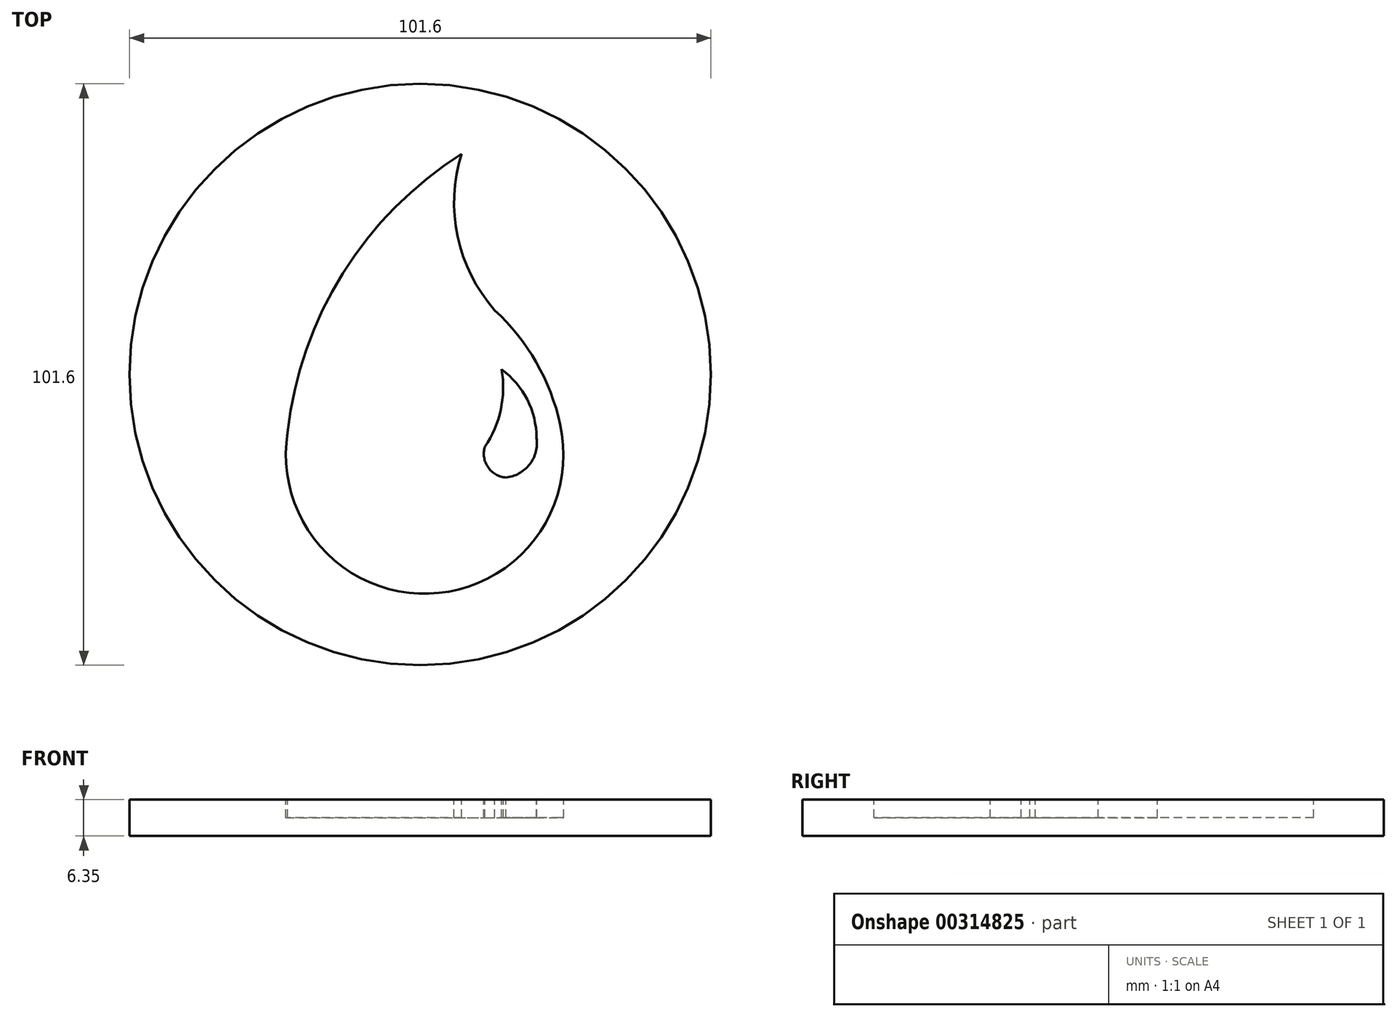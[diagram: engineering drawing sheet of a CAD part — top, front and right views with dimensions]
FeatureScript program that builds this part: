
annotation { "Feature Type Name" : "Feature", "Feature Type Description" : "" }
export const myFeature = defineFeature(function(context is Context, id is Id, definition is map)
    precondition{}
    {
        {
            var Q0;
            Q0=qCreatedBy(makeId("Top.planeOp"),FACE);
            var sketch = newSketch(context, id + "F0", { "sketchPlane" : qUnion([Q0])});
            skCircle(sketch, "E0", {"center": v(0, 0) * mm, "radius": 50.8 * mm});
            skSolve(sketch);
        }
        {
            var Q0;
            Q0 = qSketchRegion(id + "F0", true);
            extrude(context, id + "F1", {"entities" : qUnion([Q0]), "depth" : 6.35 * mm});
        }
        {
            var Q0;
            Q0=makeQuery(id+"F1.opExtrude","CAP_FACE",FACE,{"disambiguationData":[OSD([sQuery(id+"F0.wireOp",EDGE,"E0")])],"isStart":false});
            var sketch = newSketch(context, id + "F2", { "sketchPlane" : qUnion([Q0])});
            skArc(sketch, "E1", {"start": v(-23.17, -10.14) * mm, "mid": v(1.51, -38.29) * mm, "end": v(24.44, -8.69) * mm});
            skArc(sketch, "E2", {"start": v(7.24, 38.56) * mm, "mid": v(-13.52, 17.68) * mm, "end": v(-23.17, -10.14) * mm});
            skArc(sketch, "E3", {"start": v(24.44, -8.69) * mm, "mid": v(20.27, 2.14) * mm, "end": v(13.03, 11.22) * mm});
            skArc(sketch, "E4", {"start": v(7.24, 38.56) * mm, "mid": v(6.52, 24.12) * mm, "end": v(13.03, 11.22) * mm});
            skArc(sketch, "E5", {"start": v(20.33, -11.1) * mm, "mid": v(18.7, -4.38) * mm, "end": v(14.24, 0.9) * mm});
            skArc(sketch, "E6", {"start": v(14.95, -18) * mm, "mid": v(19.12, -15.7) * mm, "end": v(20.33, -11.1) * mm});
            skArc(sketch, "E7", {"start": v(11.29, -12.61) * mm, "mid": v(11.83, -16.18) * mm, "end": v(14.95, -18) * mm});
            skArc(sketch, "E8", {"start": v(11.29, -12.61) * mm, "mid": v(14.07, -6.14) * mm, "end": v(14.24, 0.9) * mm});
            skSolve(sketch);
        }
        {
            var Q0;
            Q0 = qSketchRegion(id + "F2", true);
            extrude(context, id + "F3", {"entities" : qUnion([Q0]), "operationType" : NewBodyOperationType.REMOVE, "oppositeDirection" : true, "depth" : 3.17 * mm});
        }
    });
